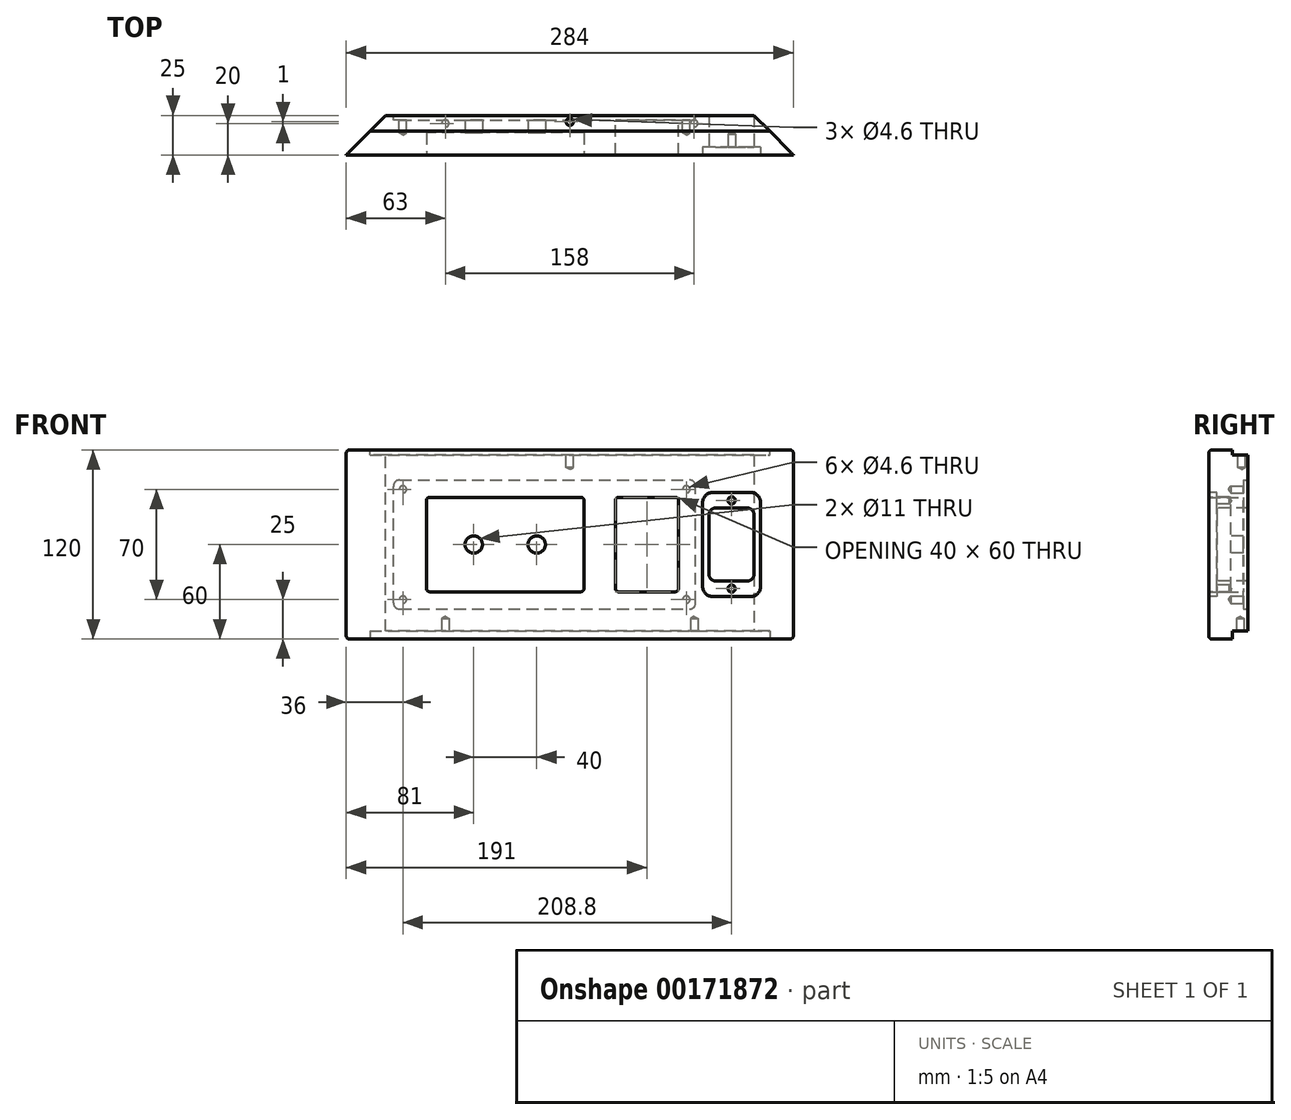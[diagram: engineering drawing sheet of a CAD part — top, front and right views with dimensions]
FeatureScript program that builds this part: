
annotation { "Feature Type Name" : "Feature", "Feature Type Description" : "" }
export const myFeature = defineFeature(function(context is Context, id is Id, definition is map)
    precondition{}
    {
        {
            var Q0;
            Q0=qCreatedBy(makeId("Front.planeOp"),FACE);
            var sketch = newSketch(context, id + "F0", { "sketchPlane" : qUnion([Q0])});
            skLineSegment(sketch, "E0.bottom", {"start": v(142, -60) * mm, "end": v(-142, -60) * mm});
            skLineSegment(sketch, "E0.top", {"start": v(142, 60) * mm, "end": v(-142, 60) * mm});
            skLineSegment(sketch, "E0.left", {"start": v(142, -60) * mm, "end": v(142, 60) * mm});
            skLineSegment(sketch, "E0.right", {"start": v(-142, -60) * mm, "end": v(-142, 60) * mm});
            skPoint(sketch, "E0.middle", {"position": v(0, 0) * mm});
            skSolve(sketch);
        }
        {
            var Q0;
            Q0=makeQuery(id+"F0.imprint","IMPRINT",FACE,{"disambiguationData":[TD([[makeQuery(id+"F0.imprint","IMPRINT",EDGE,{"derivedFrom":sQuery(id+"F0.wireOp",EDGE,"E0.bottom")}),-1.0]])]});
            extrude(context, id + "F1", {"entities" : qUnion([Q0]), "depth" : 25 * mm});
        }
        {
            var Q0;
            Q0=makeQuery(id+"F1.opExtrude","CAP_EDGE",EDGE,{"disambiguationData":[OSD([sQuery(id+"F0.wireOp",EDGE,"E0.right")])],"isStart":true});
            var Q1;
            Q1=makeQuery(id+"F1.opExtrude","CAP_EDGE",EDGE,{"disambiguationData":[OSD([sQuery(id+"F0.wireOp",EDGE,"E0.left")])],"isStart":true});
            chamfer(context, id + "F2", {"entities" : qUnion([Q0, Q1]), "width" : 25 * mm, "tangentPropagation" : true});
        }
        {
            var Q0;
            Q0=makeQuery(id+"F1.opExtrude","SWEPT_FACE",FACE,{"disambiguationData":[OSD([sQuery(id+"F0.wireOp",EDGE,"E0.top")])]});
            var sketch = newSketch(context, id + "F3", { "sketchPlane" : qUnion([Q0])});
            skLineSegment(sketch, "E1", {"start": v(-127, -10) * mm, "end": v(127, -10) * mm});
            skSolve(sketch);
        }
        {
            var Q0;
            {var subQ0=sQuery(id+"F3.wireOp",EDGE,"E1");Q0=makeQuery(id+"F3.imprint","IMPRINT",FACE,{"disambiguationData":[TD([[makeQuery(id+"F3.imprint","IMPRINT",EDGE,{"derivedFrom":subQ0}),1.0]])]});}
            extrude(context, id + "F4", {"entities" : qUnion([Q0]), "operationType" : NewBodyOperationType.REMOVE, "oppositeDirection" : true, "depth" : 3 * mm});
        }
        {
            var Q0;
            Q0=makeQuery(id+"F1.opExtrude","SWEPT_FACE",FACE,{"disambiguationData":[OSD([sQuery(id+"F0.wireOp",EDGE,"E0.bottom")])]});
            var sketch = newSketch(context, id + "F5", { "sketchPlane" : qUnion([Q0])});
            skLineSegment(sketch, "E2", {"start": v(-127, 10) * mm, "end": v(127, 10) * mm});
            skSolve(sketch);
        }
        {
            var Q0;
            {var subQ0=sQuery(id+"F5.wireOp",EDGE,"E2");Q0=makeQuery(id+"F5.imprint","IMPRINT",FACE,{"disambiguationData":[TD([[makeQuery(id+"F5.imprint","IMPRINT",EDGE,{"derivedFrom":subQ0}),-1.0]])]});}
            extrude(context, id + "F6", {"entities" : qUnion([Q0]), "operationType" : NewBodyOperationType.REMOVE, "oppositeDirection" : true, "depth" : 5 * mm});
        }
        {
            var Q0;
            Q0=makeQuery(id+"F1.opExtrude","CAP_FACE",FACE,{"disambiguationData":[OSD([sQuery(id+"F0.wireOp",EDGE,"E0.bottom"),sQuery(id+"F0.wireOp",EDGE,"E0.top"),sQuery(id+"F0.wireOp",EDGE,"E0.left"),sQuery(id+"F0.wireOp",EDGE,"E0.right")])],"isStart":false});
            var sketch = newSketch(context, id + "F7", { "sketchPlane" : qUnion([Q0])});
            skLineSegment(sketch, "E3.bottom", {"start": v(92.5, 23.15) * mm, "end": v(113, 23.15) * mm});
            skLineSegment(sketch, "E3.top", {"start": v(92.5, -23.15) * mm, "end": v(113, -23.15) * mm});
            skLineSegment(sketch, "E3.left", {"start": v(88.5, 19.15) * mm, "end": v(88.5, -19.15) * mm});
            skLineSegment(sketch, "E3.right", {"start": v(117, 19.15) * mm, "end": v(117, -19.15) * mm});
            skLineSegment(sketch, "E4", {"start": v(0, 0) * mm, "end": v(92, 0) * mm, "construction": true});
            skPoint(sketch, "E5.visualSharp", {"position": v(117, 23.15) * mm});
            skArc(sketch, "E5.filletArc", {"start": v(117, 19.15) * mm, "mid": v(115.83, 21.98) * mm, "end": v(113, 23.15) * mm});
            skPoint(sketch, "E6.visualSharp", {"position": v(88.5, 23.15) * mm});
            skArc(sketch, "E6.filletArc", {"start": v(92.5, 23.15) * mm, "mid": v(89.67, 21.98) * mm, "end": v(88.5, 19.15) * mm});
            skPoint(sketch, "E7.visualSharp", {"position": v(88.5, -23.15) * mm});
            skArc(sketch, "E7.filletArc", {"start": v(88.5, -19.15) * mm, "mid": v(89.67, -21.98) * mm, "end": v(92.5, -23.15) * mm});
            skPoint(sketch, "E8.visualSharp", {"position": v(117, -23.15) * mm});
            skArc(sketch, "E8.filletArc", {"start": v(113, -23.15) * mm, "mid": v(115.83, -21.98) * mm, "end": v(117, -19.15) * mm});
            skLineSegment(sketch, "E9.bottom", {"start": v(114.7, -33.1) * mm, "end": v(90.9, -33.1) * mm});
            skLineSegment(sketch, "E9.top", {"start": v(114.7, 33.1) * mm, "end": v(90.9, 33.1) * mm});
            skLineSegment(sketch, "E9.left", {"start": v(121.2, -26.6) * mm, "end": v(121.2, 26.6) * mm});
            skLineSegment(sketch, "E9.right", {"start": v(84.4, -26.6) * mm, "end": v(84.4, 26.6) * mm});
            skPoint(sketch, "E9.middle", {"position": v(102.8, 0) * mm});
            skPoint(sketch, "E10.visualSharp", {"position": v(84.4, 33.1) * mm});
            skArc(sketch, "E10.filletArc", {"start": v(90.9, 33.1) * mm, "mid": v(86.3, 31.2) * mm, "end": v(84.4, 26.6) * mm});
            skPoint(sketch, "E11.visualSharp", {"position": v(121.2, 33.1) * mm});
            skArc(sketch, "E11.filletArc", {"start": v(121.2, 26.6) * mm, "mid": v(119.3, 31.2) * mm, "end": v(114.7, 33.1) * mm});
            skPoint(sketch, "E12.visualSharp", {"position": v(121.2, -33.1) * mm});
            skArc(sketch, "E12.filletArc", {"start": v(114.7, -33.1) * mm, "mid": v(119.3, -31.2) * mm, "end": v(121.2, -26.6) * mm});
            skPoint(sketch, "E13.visualSharp", {"position": v(84.4, -33.1) * mm});
            skArc(sketch, "E13.filletArc", {"start": v(84.4, -26.6) * mm, "mid": v(86.3, -31.2) * mm, "end": v(90.9, -33.1) * mm});
            skSolve(sketch);
        }
        {
            var Q0;
            Q0=makeQuery(id+"F7.imprint","IMPRINT",FACE,{"disambiguationData":[TD([[makeQuery(id+"F7.imprint","IMPRINT",EDGE,{"derivedFrom":sQuery(id+"F7.wireOp",EDGE,"E3.bottom")}),-1.0]])]});
            extrude(context, id + "F8", {"entities" : qUnion([Q0]), "operationType" : NewBodyOperationType.REMOVE, "endBound" : BoundingType.THROUGH_ALL, "oppositeDirection" : true, "depth" : 25 * mm});
        }
        {
            var Q0;
            Q0=makeQuery(id+"F0.imprint","IMPRINT",FACE,{"disambiguationData":[TD([[makeQuery(id+"F0.imprint","IMPRINT",EDGE,{"derivedFrom":sQuery(id+"F0.wireOp",EDGE,"E0.bottom")}),-1.0]])]});
            var sketch = newSketch(context, id + "F9", { "sketchPlane" : qUnion([Q0])});
            skLineSegment(sketch, "E14.bottom", {"start": v(-108, -41) * mm, "end": v(76, -41) * mm});
            skLineSegment(sketch, "E14.top", {"start": v(-108, 41) * mm, "end": v(76, 41) * mm});
            skLineSegment(sketch, "E14.left", {"start": v(-112, -37) * mm, "end": v(-112, 37) * mm});
            skLineSegment(sketch, "E14.right", {"start": v(80, -37) * mm, "end": v(80, 37) * mm});
            skPoint(sketch, "E14.middle", {"position": v(-16, 0) * mm});
            skPoint(sketch, "E15.visualSharp", {"position": v(80, 41) * mm});
            skArc(sketch, "E15.filletArc", {"start": v(80, 37) * mm, "mid": v(78.83, 39.83) * mm, "end": v(76, 41) * mm});
            skPoint(sketch, "E16.visualSharp", {"position": v(-112, 41) * mm});
            skArc(sketch, "E16.filletArc", {"start": v(-108, 41) * mm, "mid": v(-110.83, 39.83) * mm, "end": v(-112, 37) * mm});
            skPoint(sketch, "E17.visualSharp", {"position": v(-112, -41) * mm});
            skArc(sketch, "E17.filletArc", {"start": v(-112, -37) * mm, "mid": v(-110.83, -39.83) * mm, "end": v(-108, -41) * mm});
            skPoint(sketch, "E18.visualSharp", {"position": v(80, -41) * mm});
            skArc(sketch, "E18.filletArc", {"start": v(76, -41) * mm, "mid": v(78.83, -39.83) * mm, "end": v(80, -37) * mm});
            skLineSegment(sketch, "E19.bottom", {"start": v(67, 30) * mm, "end": v(31, 30) * mm});
            skLineSegment(sketch, "E19.top", {"start": v(67, -30) * mm, "end": v(31, -30) * mm});
            skLineSegment(sketch, "E19.left", {"start": v(69, 28) * mm, "end": v(69, -28) * mm});
            skLineSegment(sketch, "E19.right", {"start": v(29, 28) * mm, "end": v(29, -28) * mm});
            skPoint(sketch, "E20.visualSharp", {"position": v(69, 30) * mm});
            skArc(sketch, "E20.filletArc", {"start": v(69, 28) * mm, "mid": v(68.41, 29.41) * mm, "end": v(67, 30) * mm});
            skPoint(sketch, "E21.visualSharp", {"position": v(29, 30) * mm});
            skArc(sketch, "E21.filletArc", {"start": v(31, 30) * mm, "mid": v(29.59, 29.41) * mm, "end": v(29, 28) * mm});
            skPoint(sketch, "E22.visualSharp", {"position": v(29, -30) * mm});
            skArc(sketch, "E22.filletArc", {"start": v(29, -28) * mm, "mid": v(29.59, -29.41) * mm, "end": v(31, -30) * mm});
            skPoint(sketch, "E23.visualSharp", {"position": v(69, -30) * mm});
            skArc(sketch, "E23.filletArc", {"start": v(67, -30) * mm, "mid": v(68.41, -29.41) * mm, "end": v(69, -28) * mm});
            skSolve(sketch);
        }
        {
            var Q0;
            Q0=qSketchRegion(id+"F9",true);
            extrude(context, id + "F10", {"entities" : qUnion([Q0]), "operationType" : NewBodyOperationType.REMOVE, "depth" : 3 * mm});
        }
        {
            var Q0;
            Q0=makeQuery(id+"F7.imprint","IMPRINT",FACE,{"disambiguationData":[TD([[makeQuery(id+"F7.imprint","IMPRINT",EDGE,{"derivedFrom":sQuery(id+"F7.wireOp",EDGE,"E3.bottom")}),1.0]])]});
            extrude(context, id + "F11", {"entities" : qUnion([Q0]), "operationType" : NewBodyOperationType.REMOVE, "oppositeDirection" : true, "depth" : 5.1 * mm});
        }
        {
            var Q0;
            Q0=makeQuery(id+"F11.boolean.opBoolean","COPY",FACE,{"derivedFrom":makeQuery(id+"F11.opExtrude","CAP_FACE",FACE,{"disambiguationData":[OSD([sQuery(id+"F7.wireOp",EDGE,"E3.bottom"),sQuery(id+"F7.wireOp",EDGE,"E3.top"),sQuery(id+"F7.wireOp",EDGE,"E3.left"),sQuery(id+"F7.wireOp",EDGE,"E3.right"),sQuery(id+"F7.wireOp",EDGE,"E5.filletArc"),sQuery(id+"F7.wireOp",EDGE,"E6.filletArc"),sQuery(id+"F7.wireOp",EDGE,"E7.filletArc"),sQuery(id+"F7.wireOp",EDGE,"E8.filletArc"),sQuery(id+"F7.wireOp",EDGE,"E9.bottom"),sQuery(id+"F7.wireOp",EDGE,"E9.top"),sQuery(id+"F7.wireOp",EDGE,"E9.left"),sQuery(id+"F7.wireOp",EDGE,"E9.right"),sQuery(id+"F7.wireOp",EDGE,"E10.filletArc"),sQuery(id+"F7.wireOp",EDGE,"E11.filletArc"),sQuery(id+"F7.wireOp",EDGE,"E12.filletArc"),sQuery(id+"F7.wireOp",EDGE,"E13.filletArc")])],"isStart":false})});
            var sketch = newSketch(context, id + "F12", { "sketchPlane" : qUnion([Q0])});
            skLineSegment(sketch, "E24", {"start": v(102.8, 36.2) * mm, "end": v(102.8, 16.23) * mm, "construction": true});
            skLineSegment(sketch, "E25", {"start": v(79.7, 28) * mm, "end": v(125.49, 28) * mm, "construction": true});
            skLineSegment(sketch, "E26", {"start": v(81.27, -28) * mm, "end": v(123.54, -28) * mm, "construction": true});
            skLineSegment(sketch, "E27", {"start": v(102.8, -21.46) * mm, "end": v(102.8, -30.65) * mm, "construction": true});
            skPoint(sketch, "E28", {"position": v(102.8, 28) * mm});
            skPoint(sketch, "E29", {"position": v(102.8, -28) * mm});
            skSolve(sketch);
        }
        {
            var Q0;
            Q0=sQuery(id+"F12.wireOp",VERTEX,"E28");
            var Q1;
            Q1=sQuery(id+"F12.wireOp",VERTEX,"E29");
            var Q2;
            Q2=makeQuery(id+"F1.opExtrude","SWEPT_BODY",BODY,{"disambiguationData":[OSD([sQuery(id+"F0.wireOp",EDGE,"E0.bottom"),sQuery(id+"F0.wireOp",EDGE,"E0.top"),sQuery(id+"F0.wireOp",EDGE,"E0.left"),sQuery(id+"F0.wireOp",EDGE,"E0.right")])]});
            hole(context, id + "F13", {"style" : HoleStyle.SIMPLE, "endStyle" : HoleEndStyle.BLIND, "holeDiameter" : 4.6 * mm, "holeDepth" : 8 * mm, "startFromSketch" : true, "locations" : qUnion([Q0, Q1]), "scope" : qUnion([Q2])});
        }
        {
            var Q0;
            Q0=makeQuery(id+"F10.boolean.opBoolean","SPLIT",FACE,{"disambiguationData":[TD([makeQuery(id+"F10.opExtrude","SWEPT_FACE",FACE,{"disambiguationData":[OSD([sQuery(id+"F9.wireOp",EDGE,"4pARmDZG-V61u-O6GJ-PLlb-et7QuPjkOFyp.bottom")])]})])],"derivedFrom":makeQuery(id+"F1.opExtrude","CAP_FACE",FACE,{"disambiguationData":[OSD([sQuery(id+"F0.wireOp",EDGE,"E0.bottom"),sQuery(id+"F0.wireOp",EDGE,"E0.top"),sQuery(id+"F0.wireOp",EDGE,"E0.left"),sQuery(id+"F0.wireOp",EDGE,"E0.right")])],"isStart":true})});
            var Q1;
            Q1=makeQuery(id+"F10.boolean.opBoolean","SPLIT",FACE,{"disambiguationData":[TD([makeQuery(id+"F10.opExtrude","SWEPT_FACE",FACE,{"disambiguationData":[OSD([sQuery(id+"F9.wireOp",EDGE,"E19.bottom")])]})])],"derivedFrom":makeQuery(id+"F1.opExtrude","CAP_FACE",FACE,{"disambiguationData":[OSD([sQuery(id+"F0.wireOp",EDGE,"E0.bottom"),sQuery(id+"F0.wireOp",EDGE,"E0.top"),sQuery(id+"F0.wireOp",EDGE,"E0.left"),sQuery(id+"F0.wireOp",EDGE,"E0.right")])],"isStart":true})});
            extrude(context, id + "F14", {"entities" : qUnion([Q0, Q1]), "operationType" : NewBodyOperationType.REMOVE, "endBound" : BoundingType.THROUGH_ALL, "oppositeDirection" : true, "depth" : 25 * mm});
        }
        {
            var Q0;
            Q0=makeQuery(id+"F10.boolean.opBoolean","COPY",FACE,{"derivedFrom":makeQuery(id+"F10.opExtrude","CAP_FACE",FACE,{"disambiguationData":[OSD([sQuery(id+"F9.wireOp",EDGE,"E14.bottom"),sQuery(id+"F9.wireOp",EDGE,"E14.top"),sQuery(id+"F9.wireOp",EDGE,"E14.left"),sQuery(id+"F9.wireOp",EDGE,"E14.right"),sQuery(id+"F9.wireOp",EDGE,"E15.filletArc"),sQuery(id+"F9.wireOp",EDGE,"E16.filletArc"),sQuery(id+"F9.wireOp",EDGE,"E17.filletArc"),sQuery(id+"F9.wireOp",EDGE,"E18.filletArc"),sQuery(id+"F9.wireOp",EDGE,"4pARmDZG-V61u-O6GJ-PLlb-et7QuPjkOFyp.bottom"),sQuery(id+"F9.wireOp",EDGE,"4pARmDZG-V61u-O6GJ-PLlb-et7QuPjkOFyp.top"),sQuery(id+"F9.wireOp",EDGE,"4pARmDZG-V61u-O6GJ-PLlb-et7QuPjkOFyp.left"),sQuery(id+"F9.wireOp",EDGE,"4pARmDZG-V61u-O6GJ-PLlb-et7QuPjkOFyp.right"),sQuery(id+"F9.wireOp",EDGE,"5d03931e-63c1-4951-b6ba-6f22913cc0ef.filletArc"),sQuery(id+"F9.wireOp",EDGE,"92cf5d46-93f2-4fa6-a040-7da8407b93e0.filletArc"),sQuery(id+"F9.wireOp",EDGE,"c2488a77-520b-4906-acd9-0cd7790adfcf.filletArc"),sQuery(id+"F9.wireOp",EDGE,"37401de3-2acb-40b5-926e-83b37fa8c636.filletArc")])],"isStart":false})});
            var sketch = newSketch(context, id + "F15", { "sketchPlane" : qUnion([Q0])});
            skLineSegment(sketch, "E30", {"start": v(-74, 45.92) * mm, "end": v(-74, -54.76) * mm, "construction": true});
            skLineSegment(sketch, "E31", {"start": v(106, 50.84) * mm, "end": v(106, -52.8) * mm, "construction": true});
            skLineSegment(sketch, "E32", {"start": v(-88.36, 35) * mm, "end": v(119.3, 35) * mm, "construction": true});
            skLineSegment(sketch, "E33", {"start": v(-86.86, -35) * mm, "end": v(123.65, -35) * mm, "construction": true});
            skPoint(sketch, "E34", {"position": v(-74, 35) * mm});
            skPoint(sketch, "E35", {"position": v(106, 35) * mm});
            skPoint(sketch, "E36", {"position": v(106, -35) * mm});
            skPoint(sketch, "E37", {"position": v(-74, -35) * mm});
            skSolve(sketch);
        }
        {
            var Q0;
            Q0=sQuery(id+"F15.wireOp",VERTEX,"E34");
            var Q1;
            Q1=sQuery(id+"F15.wireOp",VERTEX,"E35");
            var Q2;
            Q2=sQuery(id+"F15.wireOp",VERTEX,"E36");
            var Q3;
            Q3=sQuery(id+"F15.wireOp",VERTEX,"E37");
            var Q4;
            Q4=makeQuery(id+"F1.opExtrude","SWEPT_BODY",BODY,{"disambiguationData":[OSD([sQuery(id+"F0.wireOp",EDGE,"E0.bottom"),sQuery(id+"F0.wireOp",EDGE,"E0.top"),sQuery(id+"F0.wireOp",EDGE,"E0.left"),sQuery(id+"F0.wireOp",EDGE,"E0.right")])]});
            hole(context, id + "F16", {"style" : HoleStyle.SIMPLE, "endStyle" : HoleEndStyle.BLIND, "holeDiameter" : 4.6 * mm, "holeDepth" : 8 * mm, "startFromSketch" : true, "locations" : qUnion([Q0, Q1, Q2, Q3]), "scope" : qUnion([Q4])});
        }
        {
            var Q0;
            Q0=makeQuery(id+"F4.boolean.opBoolean","COPY",FACE,{"derivedFrom":makeQuery(id+"F4.opExtrude","CAP_FACE",FACE,{"disambiguationData":[OSD([sQuery(id+"F0.wireOp",EDGE,"E0.top"),sQuery(id+"F0.wireOp",EDGE,"E0.left"),sQuery(id+"F0.wireOp",EDGE,"E0.right"),sQuery(id+"F3.wireOp",EDGE,"E1")])],"isStart":false})});
            var sketch = newSketch(context, id + "F17", { "sketchPlane" : qUnion([Q0])});
            skLineSegment(sketch, "E38", {"start": v(-125.51, -4) * mm, "end": v(119.08, -4) * mm, "construction": true});
            skLineSegment(sketch, "E39", {"start": v(0, 6.88) * mm, "end": v(0, -25.49) * mm, "construction": true});
            skPoint(sketch, "E39.endSnap0", {"position": v(0, -10) * mm});
            skPoint(sketch, "E40", {"position": v(0, -4) * mm});
            skSolve(sketch);
        }
        {
            var Q0;
            Q0=sQuery(id+"F17.wireOp",VERTEX,"E40");
            var Q1;
            Q1=makeQuery(id+"F1.opExtrude","SWEPT_BODY",BODY,{"disambiguationData":[OSD([sQuery(id+"F0.wireOp",EDGE,"E0.bottom"),sQuery(id+"F0.wireOp",EDGE,"E0.top"),sQuery(id+"F0.wireOp",EDGE,"E0.left"),sQuery(id+"F0.wireOp",EDGE,"E0.right")])]});
            hole(context, id + "F18", {"style" : HoleStyle.SIMPLE, "endStyle" : HoleEndStyle.BLIND, "holeDiameter" : 4.6 * mm, "holeDepth" : 8 * mm, "startFromSketch" : true, "locations" : qUnion([Q0]), "scope" : qUnion([Q1])});
        }
        {
            var Q0;
            Q0=makeQuery(id+"F6.boolean.opBoolean","COPY",FACE,{"derivedFrom":makeQuery(id+"F6.opExtrude","CAP_FACE",FACE,{"disambiguationData":[OSD([sQuery(id+"F0.wireOp",EDGE,"E0.bottom"),sQuery(id+"F0.wireOp",EDGE,"E0.left"),sQuery(id+"F0.wireOp",EDGE,"E0.right"),sQuery(id+"F5.wireOp",EDGE,"E2")])],"isStart":false})});
            var sketch = newSketch(context, id + "F19", { "sketchPlane" : qUnion([Q0])});
            skLineSegment(sketch, "E41", {"start": v(-139.49, 5) * mm, "end": v(132.14, 5) * mm, "construction": true});
            skPoint(sketch, "E41.endSnap0", {"position": v(122, 5) * mm});
            skLineSegment(sketch, "E42", {"start": v(-79, 19.2) * mm, "end": v(-79, -13.88) * mm, "construction": true});
            skLineSegment(sketch, "E43", {"start": v(0, 25.09) * mm, "end": v(0, -14.6) * mm, "construction": true});
            skLineSegment(sketch, "E44", {"start": v(79, 23.98) * mm, "end": v(79, -15.34) * mm, "construction": true});
            skPoint(sketch, "E45", {"position": v(-79, 5) * mm});
            skPoint(sketch, "E46", {"position": v(0, 5) * mm});
            skPoint(sketch, "E47", {"position": v(79, 5) * mm});
            skSolve(sketch);
        }
        {
            var Q0;
            Q0=sQuery(id+"F19.wireOp",VERTEX,"E45");
            var Q1;
            Q1=sQuery(id+"F19.wireOp",VERTEX,"E47");
            var Q2;
            Q2=makeQuery(id+"F1.opExtrude","SWEPT_BODY",BODY,{"disambiguationData":[OSD([sQuery(id+"F0.wireOp",EDGE,"E0.bottom"),sQuery(id+"F0.wireOp",EDGE,"E0.top"),sQuery(id+"F0.wireOp",EDGE,"E0.left"),sQuery(id+"F0.wireOp",EDGE,"E0.right")])]});
            hole(context, id + "F20", {"style" : HoleStyle.SIMPLE, "endStyle" : HoleEndStyle.BLIND, "holeDiameter" : 4.6 * mm, "holeDepth" : 8 * mm, "startFromSketch" : true, "locations" : qUnion([Q0, Q1]), "scope" : qUnion([Q2])});
        }
        {
            var Q0;
            Q0=makeQuery(id+"F1.opExtrude","CAP_EDGE",EDGE,{"disambiguationData":[OSD([sQuery(id+"F0.wireOp",EDGE,"E0.top")])],"isStart":false});
            var Q1;
            Q1=makeQuery(id+"F1.opExtrude","CAP_EDGE",EDGE,{"disambiguationData":[OSD([sQuery(id+"F0.wireOp",EDGE,"E0.bottom")])],"isStart":false});
            fillet(context, id + "F21", {"entities" : qUnion([Q0, Q1]), "radius" : 2 * mm, "tangentPropagation" : true, "allowEdgeOverflow" : false});
        }
        {
            var Q0;
            Q0=makeQuery(id+"F1.opExtrude","CAP_FACE",FACE,{"disambiguationData":[OSD([sQuery(id+"F0.wireOp",EDGE,"E0.bottom"),sQuery(id+"F0.wireOp",EDGE,"E0.top"),sQuery(id+"F0.wireOp",EDGE,"E0.left"),sQuery(id+"F0.wireOp",EDGE,"E0.right")])],"isStart":false});
            var sketch = newSketch(context, id + "F22", { "sketchPlane" : qUnion([Q0])});
            skLineSegment(sketch, "E48.bottom", {"start": v(7, -30) * mm, "end": v(-89, -30) * mm});
            skLineSegment(sketch, "E48.top", {"start": v(7, 30) * mm, "end": v(-89, 30) * mm});
            skLineSegment(sketch, "E48.left", {"start": v(9, -28) * mm, "end": v(9, 28) * mm});
            skLineSegment(sketch, "E48.right", {"start": v(-91, -28) * mm, "end": v(-91, 28) * mm});
            skPoint(sketch, "E48.middle", {"position": v(-41, 0) * mm});
            skPoint(sketch, "E49.visualSharp", {"position": v(-91, 30) * mm});
            skArc(sketch, "E49.filletArc", {"start": v(-89, 30) * mm, "mid": v(-90.41, 29.41) * mm, "end": v(-91, 28) * mm});
            skPoint(sketch, "E50.visualSharp", {"position": v(9, 30) * mm});
            skArc(sketch, "E50.filletArc", {"start": v(9, 28) * mm, "mid": v(8.41, 29.41) * mm, "end": v(7, 30) * mm});
            skPoint(sketch, "E51.visualSharp", {"position": v(9, -30) * mm});
            skArc(sketch, "E51.filletArc", {"start": v(7, -30) * mm, "mid": v(8.41, -29.41) * mm, "end": v(9, -28) * mm});
            skPoint(sketch, "E52.visualSharp", {"position": v(-91, -30) * mm});
            skArc(sketch, "E52.filletArc", {"start": v(-91, -28) * mm, "mid": v(-90.41, -29.41) * mm, "end": v(-89, -30) * mm});
            skLineSegment(sketch, "E53", {"start": v(-61, 26.25) * mm, "end": v(-61, -26.25) * mm, "construction": true});
            skLineSegment(sketch, "E54", {"start": v(-41, 27.93) * mm, "end": v(-41, -25.5) * mm, "construction": true});
            skLineSegment(sketch, "E55.MirrorCS", {"start": v(-21, 26.25) * mm, "end": v(-21, -26.25) * mm, "construction": true});
            skCircle(sketch, "E56", {"center": v(-61, 0) * mm, "radius": 5.5 * mm});
            skCircle(sketch, "E57.MirrorC", {"center": v(-21, 0) * mm, "radius": 5.5 * mm});
            skSolve(sketch);
        }
        {
            var Q0;
            Q0 = qSketchRegion(id + "F22", true);
            extrude(context, id + "F23", {"entities" : qUnion([Q0]), "operationType" : NewBodyOperationType.REMOVE, "oppositeDirection" : true, "depth" : 14 * mm});
        }
        {
            var Q0;
            Q0=makeQuery(id+"F23.boolean.opBoolean","SPLIT",FACE,{"disambiguationData":[TD([makeQuery(id+"F23.opExtrude","SWEPT_FACE",FACE,{"disambiguationData":[OSD([sQuery(id+"F22.wireOp",EDGE,"E56")])]})])],"derivedFrom":makeQuery(id+"F1.opExtrude","CAP_FACE",FACE,{"disambiguationData":[OSD([sQuery(id+"F0.wireOp",EDGE,"E0.bottom"),sQuery(id+"F0.wireOp",EDGE,"E0.top"),sQuery(id+"F0.wireOp",EDGE,"E0.left"),sQuery(id+"F0.wireOp",EDGE,"E0.right")])],"isStart":false})});
            var Q1;
            Q1=makeQuery(id+"F23.boolean.opBoolean","SPLIT",FACE,{"disambiguationData":[TD([makeQuery(id+"F23.opExtrude","SWEPT_FACE",FACE,{"disambiguationData":[OSD([sQuery(id+"F22.wireOp",EDGE,"E57.MirrorC")])]})])],"derivedFrom":makeQuery(id+"F1.opExtrude","CAP_FACE",FACE,{"disambiguationData":[OSD([sQuery(id+"F0.wireOp",EDGE,"E0.bottom"),sQuery(id+"F0.wireOp",EDGE,"E0.top"),sQuery(id+"F0.wireOp",EDGE,"E0.left"),sQuery(id+"F0.wireOp",EDGE,"E0.right")])],"isStart":false})});
            extrude(context, id + "F24", {"entities" : qUnion([Q0, Q1]), "operationType" : NewBodyOperationType.REMOVE, "oppositeDirection" : true, "depth" : 25 * mm});
        }
    });
